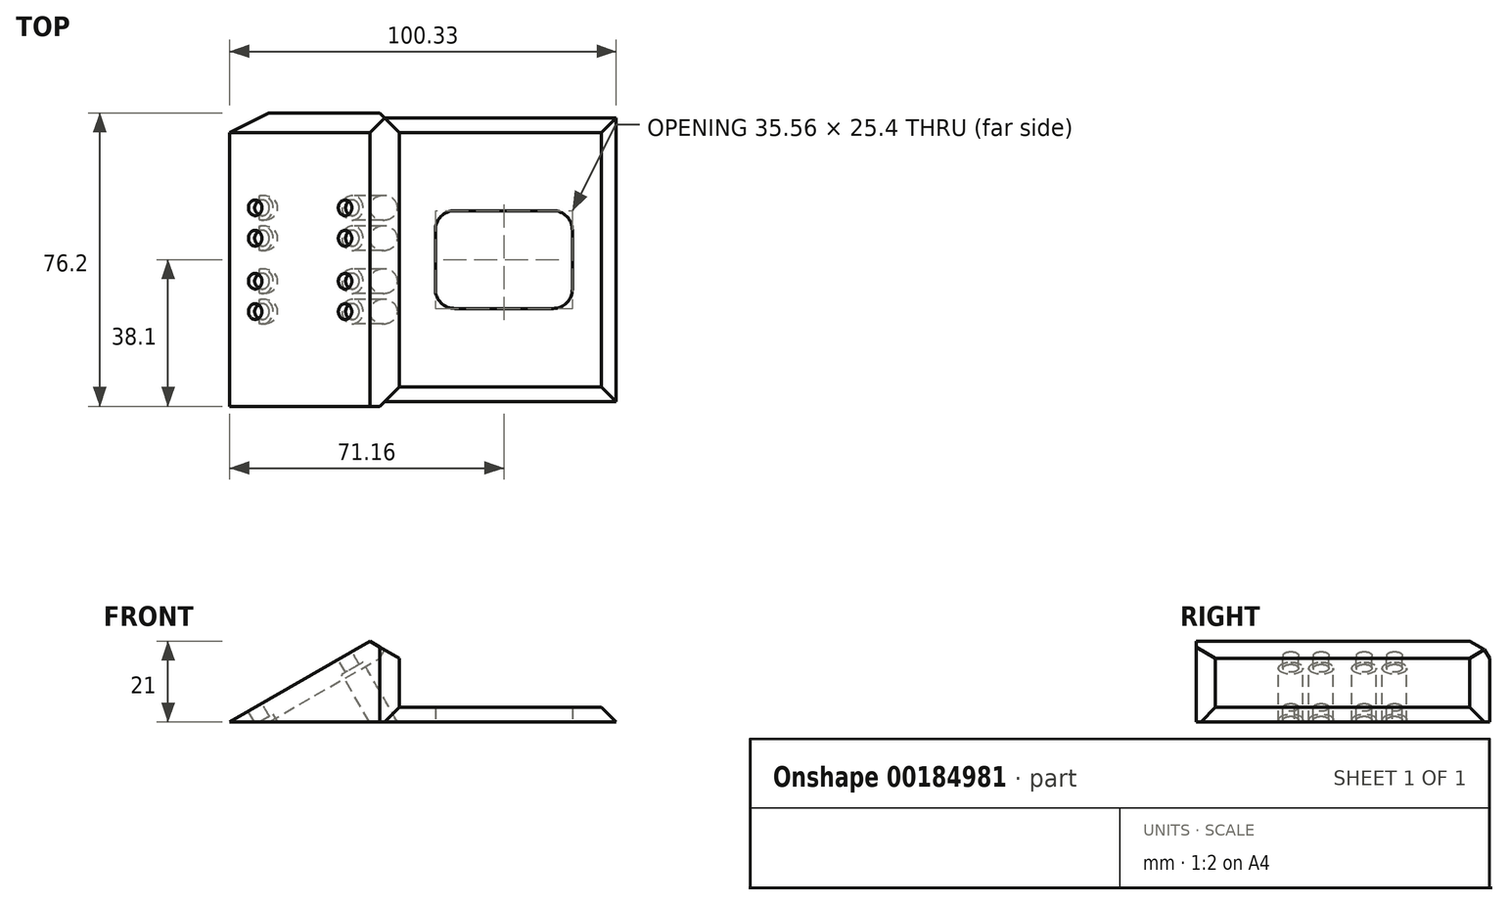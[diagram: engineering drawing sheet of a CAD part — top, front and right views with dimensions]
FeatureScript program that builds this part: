
annotation { "Feature Type Name" : "Feature", "Feature Type Description" : "" }
export const myFeature = defineFeature(function(context is Context, id is Id, definition is map)
    precondition{}
    {
        {
            var Q0;
            Q0=qCreatedBy(makeId("Top.planeOp"),FACE);
            var sketch = newSketch(context, id + "F0", { "sketchPlane" : qUnion([Q0])});
            skLineSegment(sketch, "E0.bottom", {"start": v(-88.94, 38.1) * mm, "end": v(12.66, 38.1) * mm});
            skLineSegment(sketch, "E0.top", {"start": v(-88.94, -38.1) * mm, "end": v(12.66, -38.1) * mm});
            skLineSegment(sketch, "E0.left", {"start": v(-88.94, 38.1) * mm, "end": v(-88.94, -38.1) * mm});
            skLineSegment(sketch, "E0.right", {"start": v(12.66, 38.1) * mm, "end": v(12.66, -38.1) * mm});
            skSolve(sketch);
        }
        {
            var Q0;
            Q0=qCreatedBy(makeId("Front.planeOp"),FACE);
            var sketch = newSketch(context, id + "F1", { "sketchPlane" : qUnion([Q0])});
            skLineSegment(sketch, "E1.0.1", {"start": v(-88.94, 0) * mm, "end": v(12.66, 0) * mm});
            skLineSegment(sketch, "E1.0.3", {"start": v(12.66, 0) * mm, "end": v(-88.94, 0) * mm});
            skLineSegment(sketch, "E2", {"start": v(-88.94, 0) * mm, "end": v(-44.94, 25.4) * mm});
            skLineSegment(sketch, "E3", {"start": v(-44.94, 25.4) * mm, "end": v(-44.94, 0) * mm});
            skSolve(sketch);
        }
        {
            var Q0;
            Q0=makeQuery(id+"F0.imprint","IMPRINT",FACE,{"disambiguationData":[TD([[makeQuery(id+"F0.imprint","IMPRINT",EDGE,{"derivedFrom":sQuery(id+"F0.wireOp",EDGE,"E0.bottom")}),-1.0]])]});
            extrude(context, id + "F2", {"entities" : qUnion([Q0]), "depth" : 3.8 * mm});
        }
        {
            var Q0;
            {var subQ0=sQuery(id+"F1.wireOp",EDGE,"E2");Q0=makeQuery(id+"F1.imprint","IMPRINT",FACE,{"disambiguationData":[TD([[makeQuery(id+"F1.imprint","IMPRINT",EDGE,{"derivedFrom":subQ0}),-1.0]])]});}
            extrude(context, id + "F3", {"entities" : qUnion([Q0]), "operationType" : NewBodyOperationType.ADD, "depth" : 38.1 * mm, "hasSecondDirection" : true, "secondDirectionOppositeDirection" : true, "secondDirectionDepth" : 38.1 * mm});
        }
        {
            var Q0;
            Q0=makeQuery(id+"F3.boolean.opBoolean","MERGE",FACE,{"derivedFrom":[makeQuery(id+"F2.opExtrude","SWEPT_FACE",FACE,{"disambiguationData":[OSD([sQuery(id+"F0.wireOp",EDGE,"E0.top")])]}),makeQuery(id+"F3.opExtrude","CAP_FACE",FACE,{"disambiguationData":[OSD([sQuery(id+"F1.wireOp",EDGE,"E1.0.3"),sQuery(id+"F1.wireOp",EDGE,"E2"),sQuery(id+"F1.wireOp",EDGE,"E3")])],"isStart":false})]});
            var sketch = newSketch(context, id + "F4", { "sketchPlane" : qUnion([Q0])});
            skLineSegment(sketch, "E4.0", {"start": v(-82.34, 3.8) * mm, "end": v(-44.94, 25.4) * mm});
            skLineSegment(sketch, "E5.0", {"start": v(-88.94, 3.81) * mm, "end": v(-88.94, 0) * mm});
            skLineSegment(sketch, "E6", {"start": v(-82.34, 3.8) * mm, "end": v(-88.94, 0) * mm});
            skSolve(sketch);
        }
        {
            var Q0;
            Q0=makeQuery(id+"F4.imprint","IMPRINT",FACE,{"disambiguationData":[TD([[makeQuery(id+"F4.imprint","IMPRINT",EDGE,{"derivedFrom":sQuery(id+"F4.wireOp",EDGE,"E5.0")}),1.0]])]});
            extrude(context, id + "F5", {"entities" : qUnion([Q0]), "operationType" : NewBodyOperationType.REMOVE, "oppositeDirection" : true, "depth" : 101.6 * mm});
        }
        {
            var Q0;
            Q0=makeQuery(id+"F5.boolean.opBoolean","MERGE",FACE,{"derivedFrom":[makeQuery(id+"F3.opExtrude","SWEPT_FACE",FACE,{"disambiguationData":[OSD([sQuery(id+"F1.wireOp",EDGE,"E2")])]}),makeQuery(id+"F5.opExtrude","SWEPT_FACE",FACE,{"disambiguationData":[OSD([sQuery(id+"F4.wireOp",EDGE,"E6")])]})]});
            var sketch = newSketch(context, id + "F6", { "sketchPlane" : qUnion([Q0])});
            skCircle(sketch, "E7", {"center": v(-69.4, -13.49) * mm, "radius": 2.03 * mm});
            skCircle(sketch, "E8", {"center": v(-69.4, -5.59) * mm, "radius": 2.03 * mm});
            skCircle(sketch, "E9", {"center": v(-69.4, 5.56) * mm, "radius": 2.03 * mm});
            skCircle(sketch, "E10", {"center": v(-69.4, 13.46) * mm, "radius": 2.03 * mm});
            skCircle(sketch, "E11", {"center": v(-42.45, -13.49) * mm, "radius": 2.03 * mm});
            skCircle(sketch, "E12", {"center": v(-42.45, -5.59) * mm, "radius": 2.03 * mm});
            skCircle(sketch, "E13", {"center": v(-42.45, 5.56) * mm, "radius": 2.03 * mm});
            skCircle(sketch, "E14", {"center": v(-42.45, 13.46) * mm, "radius": 2.03 * mm});
            skSolve(sketch);
        }
        {
            var Q0;
            Q0=makeQuery(id+"F6.imprint","IMPRINT",FACE,{"disambiguationData":[TD([[makeQuery(id+"F6.imprint","IMPRINT",EDGE,{"derivedFrom":sQuery(id+"F6.wireOp",EDGE,"E7")}),1.0]])]});
            var Q1;
            Q1=makeQuery(id+"F6.imprint","IMPRINT",FACE,{"disambiguationData":[TD([[makeQuery(id+"F6.imprint","IMPRINT",EDGE,{"derivedFrom":sQuery(id+"F6.wireOp",EDGE,"E8")}),1.0]])]});
            var Q2;
            Q2=makeQuery(id+"F6.imprint","IMPRINT",FACE,{"disambiguationData":[TD([[makeQuery(id+"F6.imprint","IMPRINT",EDGE,{"derivedFrom":sQuery(id+"F6.wireOp",EDGE,"E9")}),1.0]])]});
            var Q3;
            Q3=makeQuery(id+"F6.imprint","IMPRINT",FACE,{"disambiguationData":[TD([[makeQuery(id+"F6.imprint","IMPRINT",EDGE,{"derivedFrom":sQuery(id+"F6.wireOp",EDGE,"E10")}),1.0]])]});
            var Q4;
            Q4=makeQuery(id+"F6.imprint","IMPRINT",FACE,{"disambiguationData":[TD([[makeQuery(id+"F6.imprint","IMPRINT",EDGE,{"derivedFrom":sQuery(id+"F6.wireOp",EDGE,"E14")}),1.0]])]});
            var Q5;
            Q5=makeQuery(id+"F6.imprint","IMPRINT",FACE,{"disambiguationData":[TD([[makeQuery(id+"F6.imprint","IMPRINT",EDGE,{"derivedFrom":sQuery(id+"F6.wireOp",EDGE,"E12")}),1.0]])]});
            var Q6;
            Q6=makeQuery(id+"F6.imprint","IMPRINT",FACE,{"disambiguationData":[TD([[makeQuery(id+"F6.imprint","IMPRINT",EDGE,{"derivedFrom":sQuery(id+"F6.wireOp",EDGE,"E11")}),1.0]])]});
            var Q7;
            Q7=makeQuery(id+"F6.imprint","IMPRINT",FACE,{"disambiguationData":[TD([[makeQuery(id+"F6.imprint","IMPRINT",EDGE,{"derivedFrom":sQuery(id+"F6.wireOp",EDGE,"E13")}),1.0]])]});
            extrude(context, id + "F7", {"entities" : qUnion([Q0, Q1, Q2, Q3, Q4, Q5, Q6, Q7]), "operationType" : NewBodyOperationType.REMOVE, "oppositeDirection" : true, "depth" : 25.4 * mm});
        }
        {
            var Q0;
            Q0=makeQuery(id+"F5.boolean.opBoolean","MERGE",FACE,{"derivedFrom":[makeQuery(id+"F3.opExtrude","SWEPT_FACE",FACE,{"disambiguationData":[OSD([sQuery(id+"F1.wireOp",EDGE,"E2")])]}),makeQuery(id+"F5.opExtrude","SWEPT_FACE",FACE,{"disambiguationData":[OSD([sQuery(id+"F4.wireOp",EDGE,"E6")])]})]});
            cPlane(context, id + "F8", {"entities" : qUnion([Q0]), "cplaneType" : CPlaneType.OFFSET, "offset" : 3.8 * mm, "oppositeDirection" : true, "width" : 152.4 * mm, "height" : 152.4 * mm});
        }
        {
            var Q0;
            Q0=qCreatedBy(id+"F8.planeOp",FACE);
            var sketch = newSketch(context, id + "F9", { "sketchPlane" : qUnion([Q0])});
            skCircle(sketch, "E15.0", {"center": v(-69.4, 13.46) * mm, "radius": 2.03 * mm});
            skCircle(sketch, "E16.0", {"center": v(-42.45, 13.46) * mm, "radius": 2.03 * mm});
            skCircle(sketch, "E17.0", {"center": v(-42.45, 5.56) * mm, "radius": 2.03 * mm});
            skCircle(sketch, "E18.0", {"center": v(-42.45, -5.59) * mm, "radius": 2.03 * mm});
            skCircle(sketch, "E19.0", {"center": v(-69.4, -5.59) * mm, "radius": 2.03 * mm});
            skCircle(sketch, "E20.0", {"center": v(-69.4, 5.56) * mm, "radius": 2.03 * mm});
            skCircle(sketch, "E21.0", {"center": v(-69.4, -13.49) * mm, "radius": 2.03 * mm});
            skCircle(sketch, "E22.0", {"center": v(-42.45, -13.49) * mm, "radius": 2.03 * mm});
            skCircle(sketch, "E23", {"center": v(-69.4, 13.46) * mm, "radius": 3.18 * mm});
            skCircle(sketch, "E24", {"center": v(-69.4, 5.56) * mm, "radius": 3.18 * mm});
            skCircle(sketch, "E25", {"center": v(-69.4, -5.59) * mm, "radius": 3.18 * mm});
            skCircle(sketch, "E26", {"center": v(-69.4, -13.49) * mm, "radius": 3.18 * mm});
            skCircle(sketch, "E27", {"center": v(-42.45, -5.59) * mm, "radius": 3.18 * mm});
            skCircle(sketch, "E28", {"center": v(-42.45, -13.49) * mm, "radius": 3.18 * mm});
            skCircle(sketch, "E29", {"center": v(-42.45, 5.56) * mm, "radius": 3.18 * mm});
            skCircle(sketch, "E30", {"center": v(-42.45, 13.46) * mm, "radius": 3.18 * mm});
            skSolve(sketch);
        }
        {
            var Q0;
            Q0 = qSketchRegion(id + "F9", true);
            extrude(context, id + "F10", {"entities" : qUnion([Q0]), "operationType" : NewBodyOperationType.REMOVE, "oppositeDirection" : true, "depth" : 25.4 * mm});
        }
        {
            var Q0;
            Q0=makeQuery(id+"F2.opExtrude","CAP_FACE",FACE,{"disambiguationData":[OSD([sQuery(id+"F0.wireOp",EDGE,"E0.bottom"),sQuery(id+"F0.wireOp",EDGE,"E0.top"),sQuery(id+"F0.wireOp",EDGE,"E0.left"),sQuery(id+"F0.wireOp",EDGE,"E0.right")])],"isStart":true});
            var sketch = newSketch(context, id + "F11", { "sketchPlane" : qUnion([Q0])});
            skLineSegment(sketch, "E31.bottom", {"start": v(0, -12.7) * mm, "end": v(-35.56, -12.7) * mm});
            skLineSegment(sketch, "E31.top", {"start": v(0, 12.7) * mm, "end": v(-35.56, 12.7) * mm});
            skLineSegment(sketch, "E31.left", {"start": v(0, -12.7) * mm, "end": v(0, 12.7) * mm});
            skLineSegment(sketch, "E31.right", {"start": v(-35.56, -12.7) * mm, "end": v(-35.56, 12.7) * mm});
            skSolve(sketch);
        }
        {
            var Q0;
            Q0 = qSketchRegion(id + "F11", true);
            extrude(context, id + "F12", {"entities" : qUnion([Q0]), "operationType" : NewBodyOperationType.REMOVE, "oppositeDirection" : true, "depth" : 25.4 * mm});
        }
        {
            var Q0;
            Q0=makeQuery(id+"F2.opExtrude","CAP_EDGE",EDGE,{"disambiguationData":[OSD([sQuery(id+"F0.wireOp",EDGE,"E0.right")])],"isStart":false});
            var Q1;
            {var subQ0=sQuery(id+"F0.wireOp",EDGE,"E0.right");var subQ2=sQuery(id+"F0.wireOp",EDGE,"E0.top");Q1=makeQuery(id+"F3.boolean.opBoolean","SPLIT",EDGE,{"disambiguationData":[TD([makeQuery(id+"F2.opExtrude","SWEPT_FACE",FACE,{"disambiguationData":[OSD([subQ0])]})])],"derivedFrom":makeQuery(id+"F2.opExtrude","CAP_EDGE",EDGE,{"disambiguationData":[OSD([subQ2])],"isStart":false})});}
            var Q2;
            {var subQ1=sQuery(id+"F0.wireOp",EDGE,"E0.right");var subQ2=sQuery(id+"F0.wireOp",EDGE,"E0.bottom");Q2=makeQuery(id+"F3.boolean.opBoolean","SPLIT",EDGE,{"disambiguationData":[TD([makeQuery(id+"F2.opExtrude","SWEPT_FACE",FACE,{"disambiguationData":[OSD([subQ1])]})])],"derivedFrom":makeQuery(id+"F2.opExtrude","CAP_EDGE",EDGE,{"disambiguationData":[OSD([subQ2])],"isStart":false})});}
            var Q3;
            Q3=makeQuery(id+"F3.opExtrude","CAP_EDGE",EDGE,{"disambiguationData":[OSD([sQuery(id+"F1.wireOp",EDGE,"E3")])],"isStart":true});
            chamfer(context, id + "F13", {"entities" : qUnion([Q0, Q1, Q2, Q3]), "width" : 5.08 * mm, "tangentPropagation" : true});
        }
        {
            var Q0;
            Q0=makeQuery(id+"F3.opExtrude","CAP_EDGE",EDGE,{"disambiguationData":[OSD([sQuery(id+"F1.wireOp",EDGE,"E3")])],"isStart":false});
            chamfer(context, id + "F14", {"entities" : qUnion([Q0]), "width" : 5.08 * mm, "tangentPropagation" : true});
        }
        {
            var Q0;
            Q0=makeQuery(id+"F5.boolean.opBoolean","MERGE",EDGE,{"derivedFrom":[makeQuery(id+"F3.opExtrude","CAP_EDGE",EDGE,{"disambiguationData":[OSD([sQuery(id+"F1.wireOp",EDGE,"E2")])],"isStart":false}),makeQuery(id+"F5.opExtrude","CAP_EDGE",EDGE,{"disambiguationData":[OSD([sQuery(id+"F4.wireOp",EDGE,"E6")])],"isStart":true})]});
            var Q1;
            Q1=makeQuery(id+"F3.opExtrude","SWEPT_EDGE",EDGE,{"disambiguationData":[OSD([sQuery(id+"F1.wireOp",EDGE,"E2"),sQuery(id+"F1.wireOp",EDGE,"E3")])]});
            var Q2;
            Q2=makeQuery(id+"F5.boolean.opBoolean","INTERSECT",EDGE,{"derivedFrom":[makeQuery(id+"F3.boolean.opBoolean","MERGE",FACE,{"derivedFrom":[makeQuery(id+"F2.opExtrude","SWEPT_FACE",FACE,{"disambiguationData":[OSD([sQuery(id+"F0.wireOp",EDGE,"E0.bottom")])]}),makeQuery(id+"F3.opExtrude","CAP_FACE",FACE,{"disambiguationData":[OSD([sQuery(id+"F1.wireOp",EDGE,"E1.0.3"),sQuery(id+"F1.wireOp",EDGE,"E2"),sQuery(id+"F1.wireOp",EDGE,"E3")])],"isStart":true})]}),makeQuery(id+"F5.opExtrude","SWEPT_FACE",FACE,{"disambiguationData":[OSD([sQuery(id+"F4.wireOp",EDGE,"E6")])]})]});
            chamfer(context, id + "F15", {"entities" : qUnion([Q0, Q1, Q2]), "width" : 5.08 * mm, "tangentPropagation" : true});
        }
        {
            var Q0;
            Q0=makeQuery(id+"F12.boolean.opBoolean","COPY",EDGE,{"derivedFrom":makeQuery(id+"F12.opExtrude","SWEPT_EDGE",EDGE,{"disambiguationData":[OSD([sQuery(id+"F11.wireOp",EDGE,"E31.top"),sQuery(id+"F11.wireOp",EDGE,"E31.right")])]})});
            var Q1;
            Q1=makeQuery(id+"F12.boolean.opBoolean","COPY",EDGE,{"derivedFrom":makeQuery(id+"F12.opExtrude","SWEPT_EDGE",EDGE,{"disambiguationData":[OSD([sQuery(id+"F11.wireOp",EDGE,"E31.bottom"),sQuery(id+"F11.wireOp",EDGE,"E31.right")])]})});
            var Q2;
            Q2=makeQuery(id+"F12.boolean.opBoolean","COPY",EDGE,{"derivedFrom":makeQuery(id+"F12.opExtrude","SWEPT_EDGE",EDGE,{"disambiguationData":[OSD([sQuery(id+"F11.wireOp",EDGE,"E31.bottom"),sQuery(id+"F11.wireOp",EDGE,"E31.left")])]})});
            var Q3;
            Q3=makeQuery(id+"F12.boolean.opBoolean","COPY",EDGE,{"derivedFrom":makeQuery(id+"F12.opExtrude","SWEPT_EDGE",EDGE,{"disambiguationData":[OSD([sQuery(id+"F11.wireOp",EDGE,"E31.top"),sQuery(id+"F11.wireOp",EDGE,"E31.left")])]})});
            fillet(context, id + "F16", {"entities" : qUnion([Q0, Q1, Q2, Q3]), "radius" : 5.08 * mm, "tangentPropagation" : true, "allowEdgeOverflow" : false});
        }
    });
